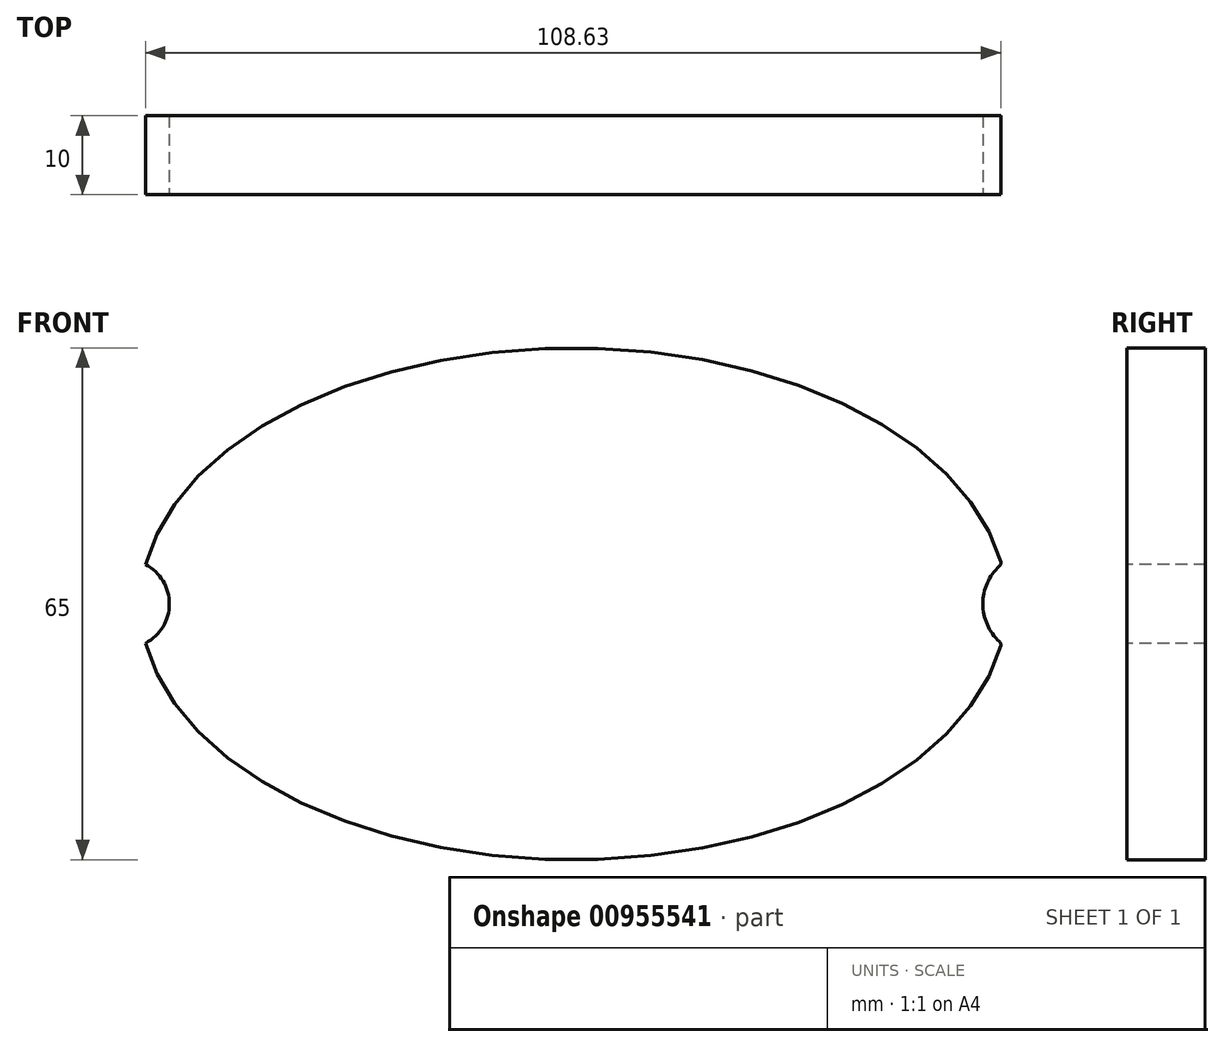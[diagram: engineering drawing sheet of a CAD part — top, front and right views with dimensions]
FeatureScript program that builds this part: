
annotation { "Feature Type Name" : "Feature", "Feature Type Description" : "" }
export const myFeature = defineFeature(function(context is Context, id is Id, definition is map)
    precondition{}
    {
        {
            var Q0;
            Q0=qCreatedBy(makeId("Front.planeOp"),FACE);
            var sketch = newSketch(context, id + "F0", { "sketchPlane" : qUnion([Q0])});
            skEllipticalArc(sketch, "E0", {});
            skArc(sketch, "E1", {"start": v(54.12, 4.8) * mm, "mid": v(52, 0) * mm, "end": v(54.12, -4.8) * mm});
            skPoint(sketch, "E2", {"position": v(52, 0) * mm});
            skPoint(sketch, "E3", {"position": v(55, 0) * mm});
            skArc(sketch, "E4.MirrorCS", {"start": v(-54.35, 5) * mm, "mid": v(-51.35, 0) * mm, "end": v(-54.35, -5) * mm});
            skEllipticalArc(sketch, "E5.trimOffspring", {});
            skPoint(sketch, "E6", {"position": v(0, 32.5) * mm});
            skEllipticalArc(sketch, "E7", {"construction": true});
            skEllipticalArc(sketch, "E8.trimOffspring", {"construction": true});
            skPoint(sketch, "E9", {"position": v(-51.35, 0) * mm});
            skPoint(sketch, "E10", {"position": v(-55, 0) * mm});
            skPoint(sketch, "E11.visualSharp", {"position": v(54.35, 5) * mm});
            skArc(sketch, "E11.filletArc", {"start": v(54.12, 4.8) * mm, "mid": v(54.26, 5.03) * mm, "end": v(54.26, 5.3) * mm});
            skPoint(sketch, "E12.visualSharp", {"position": v(54.35, -5) * mm});
            skArc(sketch, "E12.filletArc", {"start": v(54.26, -5.3) * mm, "mid": v(54.26, -5.03) * mm, "end": v(54.12, -4.8) * mm});
            const initialGuessF0  = {"E0": [0, 0, 1, 0, 0.055, 0.0325, 0.16399079683666512, 2.9871330551056094], "E5.trimOffspring": [0, 0, 1, 0, 0.055, 0.0325, 3.2960522520739755, 6.119194510342921], "E7": [0, 0, 1, 0, 0.055, 0.0325, 2.9871330551056094, 3.296052252073976], "E8.trimOffspring": [0, 0, 1, 0, 0.055, 0.0325, 6.128725708695402, 0.15445959848418375]};
            skSetInitialGuess(sketch, initialGuessF0);
            skSolve(sketch);
        }
        {
            var Q0;
            Q0=qSketchRegion(id+"F0",true);
            extrude(context, id + "F1", {"entities" : qUnion([Q0]), "oppositeDirection" : true, "depth" : 10 * mm, "offsetDistance" : 25 * mm});
        }
    });
